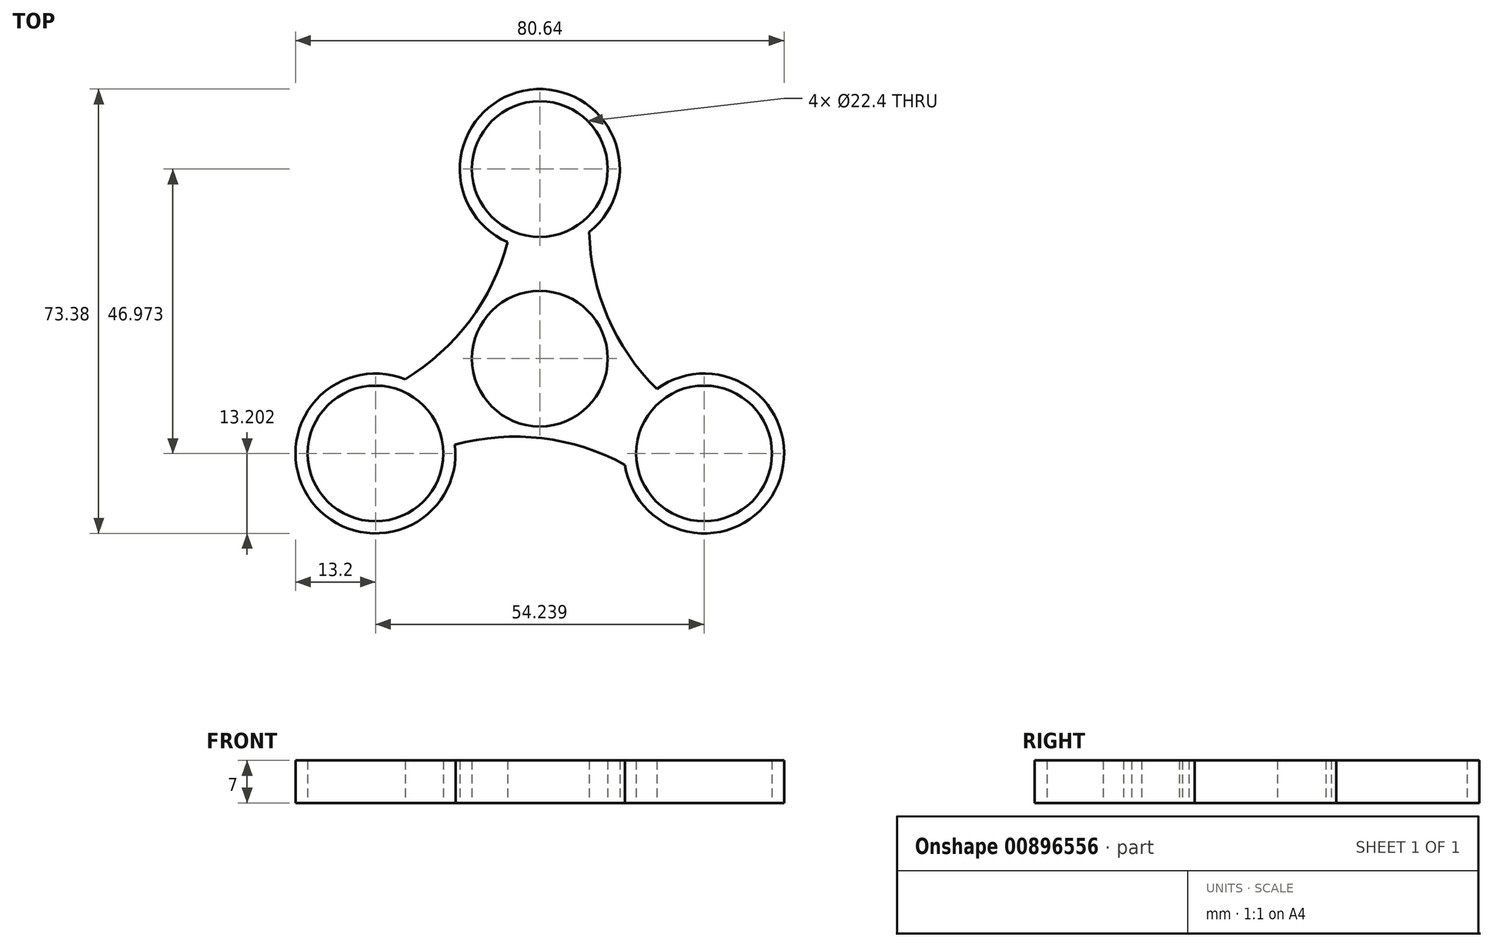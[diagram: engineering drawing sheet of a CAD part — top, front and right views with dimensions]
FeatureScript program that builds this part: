
annotation { "Feature Type Name" : "Feature", "Feature Type Description" : "" }
export const myFeature = defineFeature(function(context is Context, id is Id, definition is map)
    precondition{}
    {
        {
            var Q0;
            Q0=qCreatedBy(makeId("Top.planeOp"),FACE);
            var sketch = newSketch(context, id + "F0", { "sketchPlane" : qUnion([Q0])});
            skCircle(sketch, "E0", {"center": v(0, 0) * mm, "radius": 11.2 * mm});
            skCircle(sketch, "E1", {"center": v(0, 0) * mm, "radius": 13.2 * mm});
            skCircle(sketch, "E2", {"center": v(0, 31.32) * mm, "radius": 11.2 * mm});
            skCircle(sketch, "E3", {"center": v(0, 31.32) * mm, "radius": 13.2 * mm});
            skCircle(sketch, "E4.1.0", {"center": v(-27.12, -15.66) * mm, "radius": 11.2 * mm});
            skCircle(sketch, "E4.1.1", {"center": v(-27.12, -15.66) * mm, "radius": 13.2 * mm});
            skCircle(sketch, "E4.2.0", {"center": v(27.12, -15.66) * mm, "radius": 11.2 * mm});
            skCircle(sketch, "E4.2.1", {"center": v(27.12, -15.66) * mm, "radius": 13.2 * mm});
            skArc(sketch, "E5", {"start": v(8.17, 20.94) * mm, "mid": v(11.2, 6.88) * mm, "end": v(19.31, -5.01) * mm});
            skArc(sketch, "E6.1.0", {"start": v(-22.22, -3.4) * mm, "mid": v(-11.56, 6.27) * mm, "end": v(-5.31, 19.23) * mm});
            skArc(sketch, "E6.2.0", {"start": v(14.06, -17.54) * mm, "mid": v(0.35, -13.15) * mm, "end": v(-14, -14.22) * mm});
            skSolve(sketch);
        }
        {
            var Q0;
            Q0=makeQuery(id+"F0.imprint","IMPRINT",FACE,{"disambiguationData":[TD([[makeQuery(id+"F0.imprint","IMPRINT",EDGE,{"derivedFrom":sQuery(id+"F0.wireOp",EDGE,"E2")}),-1.0]])]});
            var Q1;
            Q1=makeQuery(id+"F0.imprint","IMPRINT",FACE,{"disambiguationData":[TD([[makeQuery(id+"F0.imprint","IMPRINT",EDGE,{"derivedFrom":sQuery(id+"F0.wireOp",EDGE,"E4.1.0")}),-1.0]])]});
            var Q2;
            Q2=makeQuery(id+"F0.imprint","IMPRINT",FACE,{"disambiguationData":[TD([[makeQuery(id+"F0.imprint","IMPRINT",EDGE,{"derivedFrom":sQuery(id+"F0.wireOp",EDGE,"E0")}),-1.0]])]});
            var Q3;
            {var subQ0=sQuery(id+"F0.wireOp",EDGE,"E5");var subQ1=sQuery(id+"F0.wireOp",EDGE,"E1");var subQ2=makeQuery(id+"F0.imprint","INTERSECT",VERTEX,{"disambiguationData":[OD(1.0)],"derivedFrom":[subQ1,subQ0]});Q3=makeQuery(id+"F0.imprint","IMPRINT",FACE,{"disambiguationData":[TD([[makeQuery(id+"F0.imprint","IMPRINT",EDGE,{"disambiguationData":[TD([[subQ2,1.0]])],"derivedFrom":subQ1}),-1.0]])]});}
            var Q4;
            Q4=makeQuery(id+"F0.imprint","IMPRINT",FACE,{"disambiguationData":[TD([[makeQuery(id+"F0.imprint","IMPRINT",EDGE,{"derivedFrom":sQuery(id+"F0.wireOp",EDGE,"E4.2.0")}),-1.0]])]});
            var Q5;
            {var subQ0=sQuery(id+"F0.wireOp",EDGE,"E5");var subQ1=sQuery(id+"F0.wireOp",EDGE,"E1");var subQ2=makeQuery(id+"F0.imprint","INTERSECT",VERTEX,{"disambiguationData":[OD(0.0)],"derivedFrom":[subQ1,subQ0]});Q5=makeQuery(id+"F0.imprint","IMPRINT",FACE,{"disambiguationData":[TD([[makeQuery(id+"F0.imprint","IMPRINT",EDGE,{"disambiguationData":[TD([[subQ2,-1.0]])],"derivedFrom":subQ1}),-1.0]])]});}
            var Q6;
            {var subQ0=sQuery(id+"F0.wireOp",EDGE,"E6.1.0");var subQ1=sQuery(id+"F0.wireOp",EDGE,"E1");var subQ2=makeQuery(id+"F0.imprint","INTERSECT",VERTEX,{"disambiguationData":[OD(1.0)],"derivedFrom":[subQ1,subQ0]});Q6=makeQuery(id+"F0.imprint","IMPRINT",FACE,{"disambiguationData":[TD([[makeQuery(id+"F0.imprint","IMPRINT",EDGE,{"disambiguationData":[TD([[subQ2,-1.0]])],"derivedFrom":subQ1}),-1.0]])]});}
            extrude(context, id + "F1", {"entities" : qUnion([Q0, Q1, Q2, Q3, Q4, Q5, Q6]), "depth" : 7 * mm, "offsetDistance" : 25 * mm});
        }
    });
